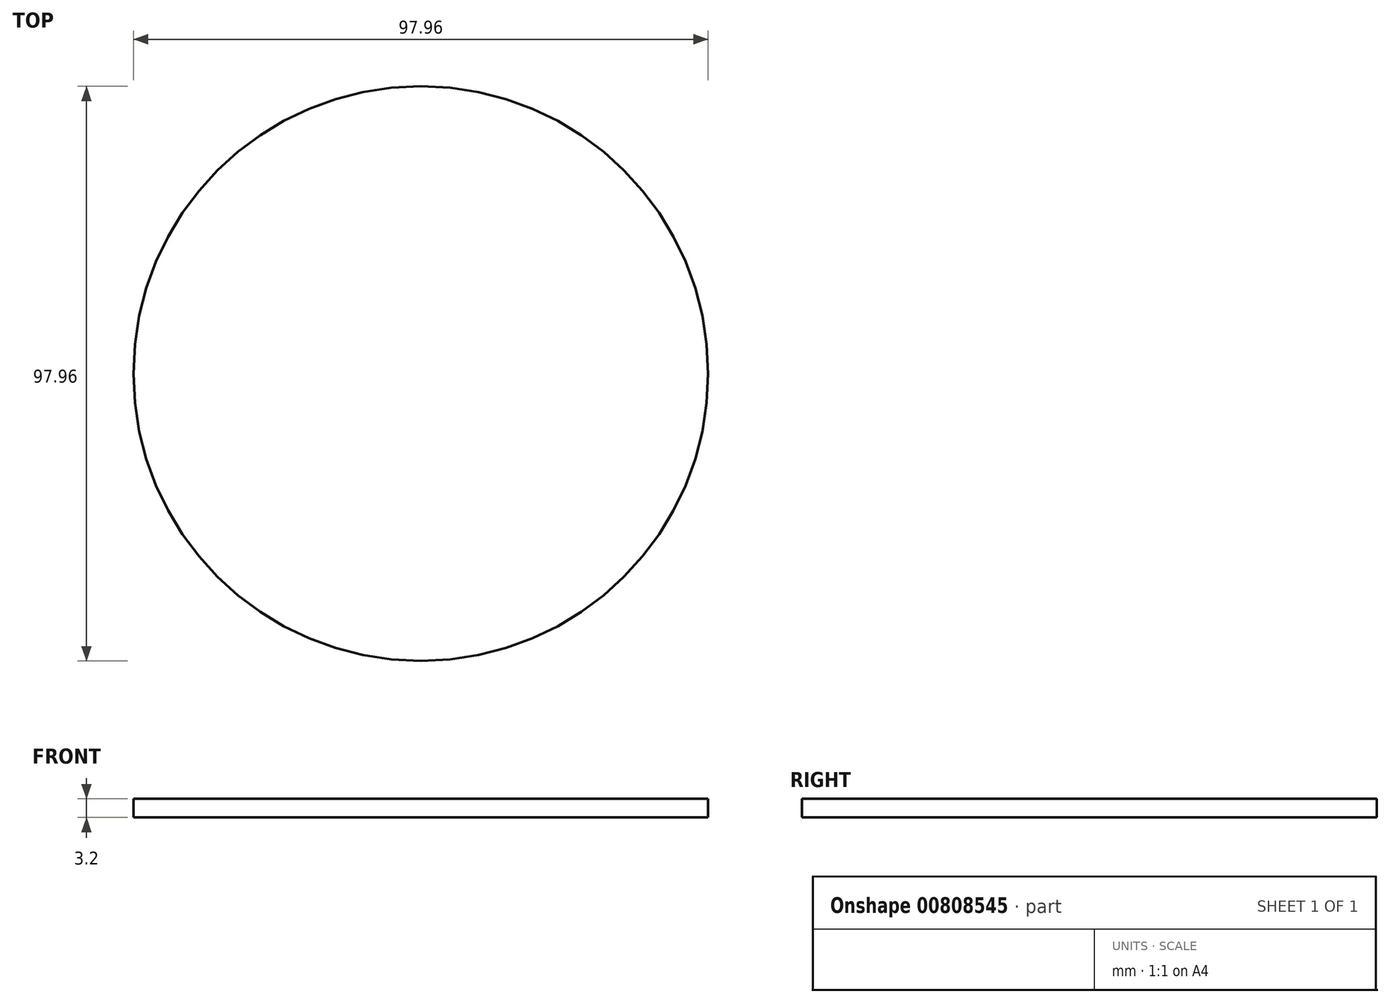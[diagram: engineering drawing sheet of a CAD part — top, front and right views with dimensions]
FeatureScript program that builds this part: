
annotation { "Feature Type Name" : "Feature", "Feature Type Description" : "" }
export const myFeature = defineFeature(function(context is Context, id is Id, definition is map)
    precondition{}
    {
        {
            var Q0;
            Q0=qCreatedBy(makeId("Top.planeOp"),FACE);
            var sketch = newSketch(context, id + "F0", { "sketchPlane" : qUnion([Q0])});
            skCircle(sketch, "E0", {"center": v(0, 0) * mm, "radius": 48.98 * mm});
            skFitSpline(sketch, "E1", {"points": [v(0, 0) * mm, v(0, 6.56) * mm, v(6.33, 7) * mm, v(13, 0) * mm, v(12.33, -6.56) * mm, v(-2.56, -12.78) * mm, v(-9.67, -7.22) * mm, v(-12.56, 0) * mm, v(-11.22, 10.11) * mm, v(-4.11, 16.34) * mm, v(13.22, 16.11) * mm, v(25.23, 7.89) * mm, v(25.9, -3) * mm, v(19.45, -19.45) * mm, v(10.78, -23.67) * mm, v(0, -23.67) * mm, v(-13.45, -22.78) * mm, v(-17.22, -12.56) * mm, v(-21, -2.11) * mm, v(-22.34, 17.67) * mm, v(-13.22, 22.78) * mm, v(0, 24.78) * mm, v(15.67, 25) * mm, v(30.78, 17.9) * mm, v(35.67, 7.89) * mm, v(28.11, -19) * mm, v(0, -36.56) * mm, v(-19.45, -34.12) * mm, v(-24.78, -22.78) * mm, v(-29.45, -13) * mm, v(-31.45, 0) * mm, v(-30.78, 18.78) * mm, v(-21.9, 29.23) * mm, v(-3.89, 36.34) * mm, v(20.11, 35.67) * mm, v(37.23, 26.34) * mm, v(43.67, 5.22) * mm, v(39, -15.9) * mm, v(23.67, -36.12) * mm, v(9.22, -43) * mm, v(-9.45, -44.12) * mm, v(-24.78, -37.67) * mm, v(-32.78, -25) * mm, v(-41.45, -9) * mm, v(-41.67, 12.78) * mm, v(-30.78, 33.23) * mm, v(-13.67, 41.23) * mm, v(-3.67, 45.23) * mm, v(6.92, 48.5) * mm], "startDerivative": vector(-123.48, 563.08) * mm, "endDerivative": vector(608.08, 167.2) * mm});
            skSolve(sketch);
        }
        {
            var Q0;
            Q0=makeQuery(id+"F0.imprint","IMPRINT",FACE,{"disambiguationData":[TD([[makeQuery(id+"F0.imprint","IMPRINT",EDGE,{"derivedFrom":sQuery(id+"F0.wireOp",EDGE,"E0")}),1.0]])]});
            extrude(context, id + "F1", {"entities" : qUnion([Q0]), "depth" : 3.2 * mm, "offsetDistance" : 25 * mm});
        }
    });
